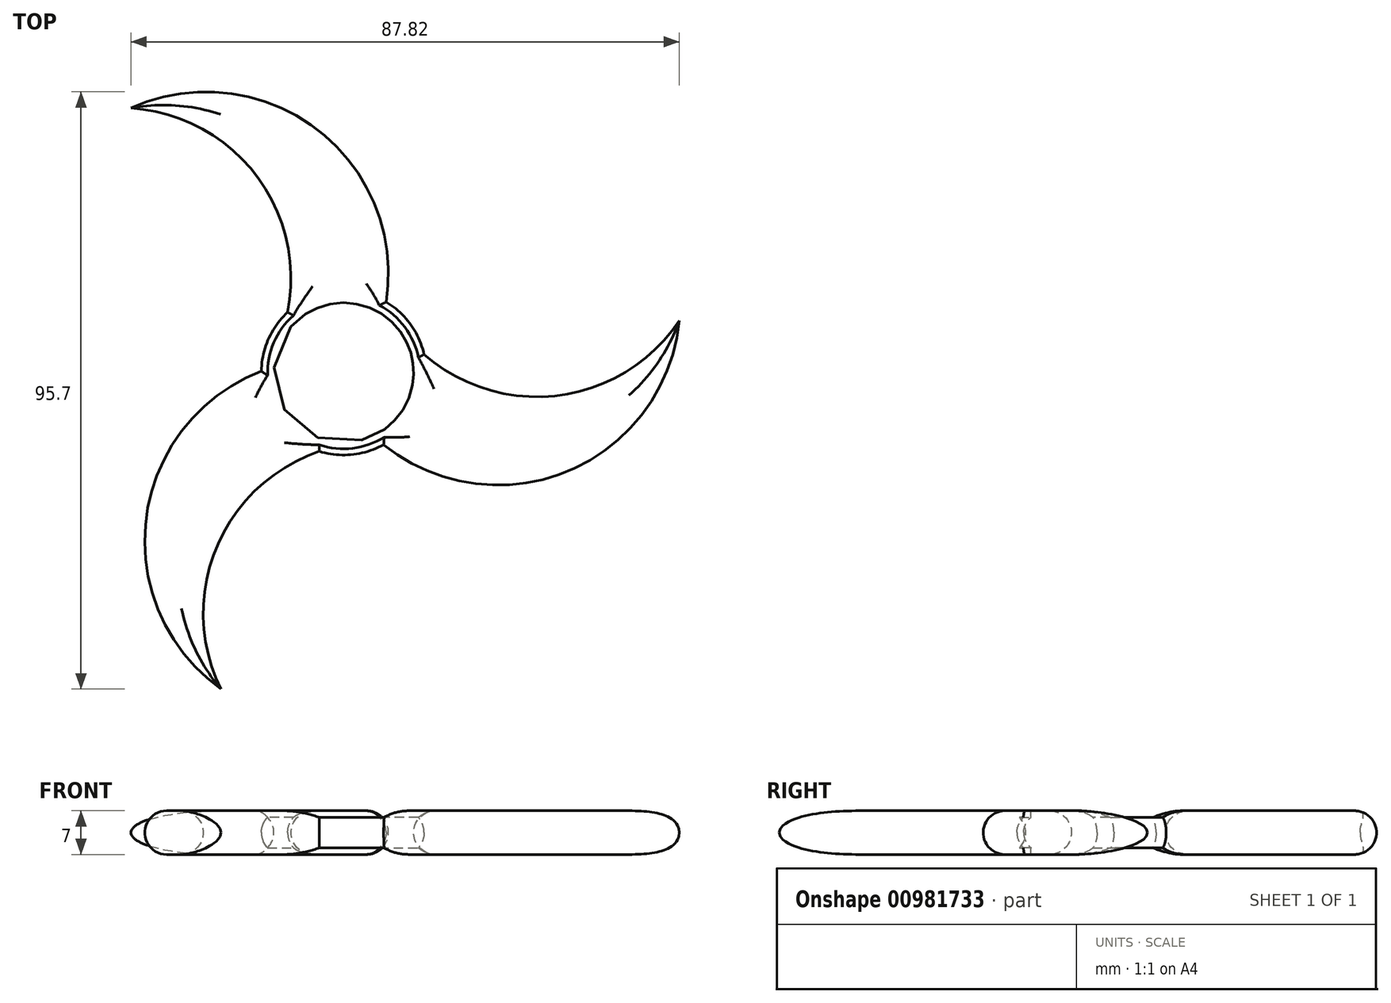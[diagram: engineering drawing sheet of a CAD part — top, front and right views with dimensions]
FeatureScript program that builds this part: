
annotation { "Feature Type Name" : "Feature", "Feature Type Description" : "" }
export const myFeature = defineFeature(function(context is Context, id is Id, definition is map)
    precondition{}
    {
        {
            var Q0;
            Q0=qCreatedBy(makeId("Top.planeOp"),FACE);
            var sketch = newSketch(context, id + "F0", { "sketchPlane" : qUnion([Q0])});
            skArc(sketch, "E0", {"start": v(-8.98, 9.68) * mm, "mid": v(-12.05, 5.39) * mm, "end": v(-13.2, 0.24) * mm});
            skArc(sketch, "E1", {"start": v(-8.98, 9.68) * mm, "mid": v(-14.11, 31.72) * mm, "end": v(-34.08, 42.38) * mm});
            skArc(sketch, "E2", {"start": v(6.8, 11.31) * mm, "mid": v(-4.36, 39.05) * mm, "end": v(-34.08, 42.38) * mm});
            skArc(sketch, "E3.1.0", {"start": v(-3.9, -12.61) * mm, "mid": v(-20.42, -28.08) * mm, "end": v(-19.67, -50.7) * mm});
            skArc(sketch, "E3.1.1", {"start": v(-13.2, 0.24) * mm, "mid": v(-31.64, -23.3) * mm, "end": v(-19.67, -50.7) * mm});
            skArc(sketch, "E3.2.0", {"start": v(12.87, 2.93) * mm, "mid": v(34.53, -3.64) * mm, "end": v(53.74, 8.32) * mm});
            skArc(sketch, "E3.2.1", {"start": v(6.4, -11.55) * mm, "mid": v(36, -15.75) * mm, "end": v(53.74, 8.32) * mm});
            skCircle(sketch, "E4", {"center": v(0, 0) * mm, "radius": 11.2 * mm});
            skArc(sketch, "E5.trimOffspring", {"start": v(12.87, 2.93) * mm, "mid": v(10.7, 7.74) * mm, "end": v(6.8, 11.31) * mm});
            skArc(sketch, "E6.trimOffspring", {"start": v(-3.9, -12.61) * mm, "mid": v(1.36, -13.13) * mm, "end": v(6.4, -11.55) * mm});
            skSolve(sketch);
        }
        {
            var Q0;
            Q0=makeQuery(id+"F0.imprint","IMPRINT",FACE,{"disambiguationData":[TD([[makeQuery(id+"F0.imprint","IMPRINT",EDGE,{"derivedFrom":sQuery(id+"F0.wireOp",EDGE,"E0")}),1.0]])]});
            extrude(context, id + "F1", {"entities" : qUnion([Q0]), "depth" : 7 * mm, "offsetDistance" : 25 * mm});
        }
        {
            var Q0;
            Q0=makeQuery(id+"F1.opExtrude","CAP_FACE",FACE,{"disambiguationData":[OSD([sQuery(id+"F0.wireOp",EDGE,"E0"),sQuery(id+"F0.wireOp",EDGE,"E1"),sQuery(id+"F0.wireOp",EDGE,"E2"),sQuery(id+"F0.wireOp",EDGE,"E3.1.0"),sQuery(id+"F0.wireOp",EDGE,"E3.1.1"),sQuery(id+"F0.wireOp",EDGE,"E3.2.0"),sQuery(id+"F0.wireOp",EDGE,"E3.2.1"),sQuery(id+"F0.wireOp",EDGE,"E4"),sQuery(id+"F0.wireOp",EDGE,"E5.trimOffspring"),sQuery(id+"F0.wireOp",EDGE,"E6.trimOffspring")])],"isStart":false});
            var Q1;
            Q1=makeQuery(id+"F1.opExtrude","CAP_FACE",FACE,{"disambiguationData":[OSD([sQuery(id+"F0.wireOp",EDGE,"E0"),sQuery(id+"F0.wireOp",EDGE,"E1"),sQuery(id+"F0.wireOp",EDGE,"E2"),sQuery(id+"F0.wireOp",EDGE,"E3.1.0"),sQuery(id+"F0.wireOp",EDGE,"E3.1.1"),sQuery(id+"F0.wireOp",EDGE,"E3.2.0"),sQuery(id+"F0.wireOp",EDGE,"E3.2.1"),sQuery(id+"F0.wireOp",EDGE,"E4"),sQuery(id+"F0.wireOp",EDGE,"E5.trimOffspring"),sQuery(id+"F0.wireOp",EDGE,"E6.trimOffspring")])],"isStart":true});
            fillet(context, id + "F2", {"entities" : qUnion([Q0, Q1]), "radius" : 3.5 * mm, "tangentPropagation" : true, "allowEdgeOverflow" : false});
        }
    });
